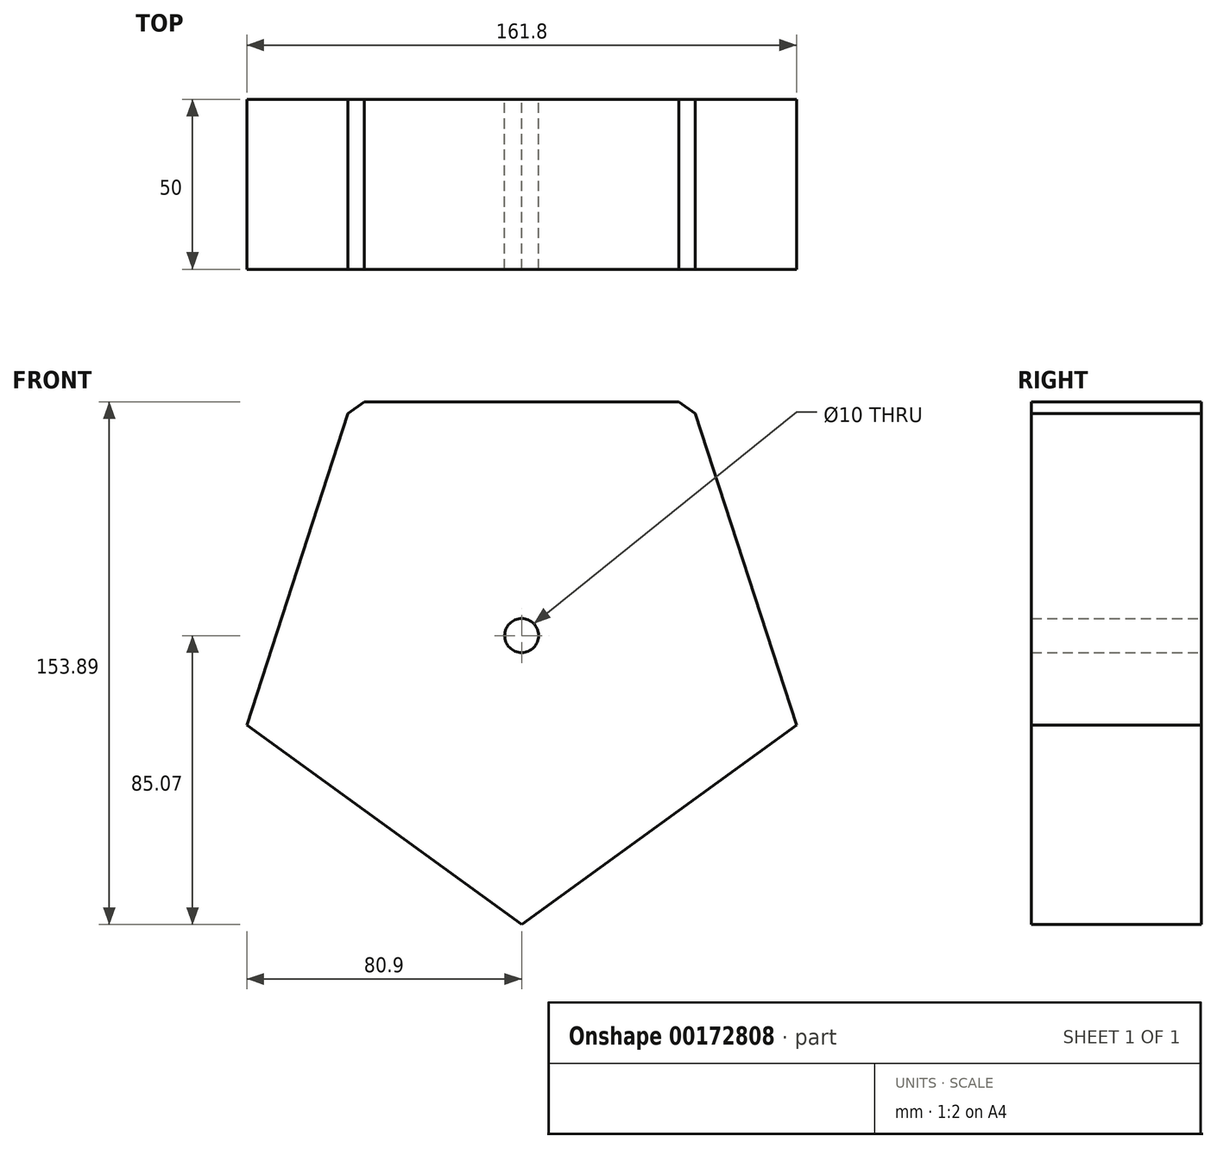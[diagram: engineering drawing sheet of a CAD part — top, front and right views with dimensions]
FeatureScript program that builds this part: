
annotation { "Feature Type Name" : "Feature", "Feature Type Description" : "" }
export const myFeature = defineFeature(function(context is Context, id is Id, definition is map)
    precondition{}
    {
        {
            var Q0;
            Q0=qCreatedBy(makeId("Front.planeOp"),FACE);
            var sketch = newSketch(context, id + "F0", { "sketchPlane" : qUnion([Q0])});
            skCircle(sketch, "E0.cCircle", {"center": v(0, 0) * mm, "radius": 68.82 * mm, "construction": true});
            skLineSegment(sketch, "E0.0", {"start": v(-50, 68.82) * mm, "end": v(50, 68.82) * mm});
            skLineSegment(sketch, "E0.1", {"start": v(50, 68.82) * mm, "end": v(80.9, -26.29) * mm});
            skLineSegment(sketch, "E0.2", {"start": v(80.9, -26.29) * mm, "end": v(0, -85.07) * mm});
            skLineSegment(sketch, "E0.3", {"start": v(0, -85.07) * mm, "end": v(-80.9, -26.29) * mm});
            skLineSegment(sketch, "E0.4", {"start": v(-80.9, -26.29) * mm, "end": v(-50, 68.82) * mm});
            skPoint(sketch, "E0.0.midPoint", {"position": v(0, 68.82) * mm});
            skSolve(sketch);
        }
        {
            var Q0;
            Q0=makeQuery(id+"F0.imprint","IMPRINT",FACE,{"disambiguationData":[TD([[makeQuery(id+"F0.imprint","IMPRINT",EDGE,{"derivedFrom":sQuery(id+"F0.wireOp",EDGE,"E0.0")}),-1.0]])]});
            extrude(context, id + "F1", {"entities" : qUnion([Q0]), "depth" : 50 * mm});
        }
        {
            var Q0;
            Q0=makeQuery(id+"F1.opExtrude","CAP_FACE",FACE,{"disambiguationData":[OSD([sQuery(id+"F0.wireOp",EDGE,"E0.0"),sQuery(id+"F0.wireOp",EDGE,"E0.1"),sQuery(id+"F0.wireOp",EDGE,"E0.2"),sQuery(id+"F0.wireOp",EDGE,"E0.3"),sQuery(id+"F0.wireOp",EDGE,"E0.4")])],"isStart":true});
            var sketch = newSketch(context, id + "F2", { "sketchPlane" : qUnion([Q0])});
            skPoint(sketch, "E1.0", {"position": v(0, 0) * mm});
            skSolve(sketch);
        }
        {
            var Q0;
            Q0=sQuery(id+"F2.wireOp",VERTEX,"E1.0");
            var Q1;
            Q1=makeQuery(id+"F1.opExtrude","SWEPT_BODY",BODY,{"disambiguationData":[OSD([sQuery(id+"F0.wireOp",EDGE,"E0.0"),sQuery(id+"F0.wireOp",EDGE,"E0.1"),sQuery(id+"F0.wireOp",EDGE,"E0.2"),sQuery(id+"F0.wireOp",EDGE,"E0.3"),sQuery(id+"F0.wireOp",EDGE,"E0.4")])]});
            hole(context, id + "F3", {"style" : HoleStyle.SIMPLE, "endStyle" : HoleEndStyle.THROUGH, "holeDiameter" : 10 * mm, "locations" : qUnion([Q0]), "scope" : qUnion([Q1]), "isTappedThrough" : true});
        }
        {
            var Q0;
            Q0=makeQuery(id+"F1.opExtrude","SWEPT_EDGE",EDGE,{"disambiguationData":[OSD([sQuery(id+"F0.wireOp",EDGE,"E0.0"),sQuery(id+"F0.wireOp",EDGE,"E0.4")])]});
            chamfer(context, id + "F4", {"entities" : qUnion([Q0]), "width" : 5 * mm, "tangentPropagation" : true});
        }
        {
            var Q0;
            Q0=makeQuery(id+"F1.opExtrude","SWEPT_EDGE",EDGE,{"disambiguationData":[OSD([sQuery(id+"F0.wireOp",EDGE,"E0.0"),sQuery(id+"F0.wireOp",EDGE,"E0.1")])]});
            chamfer(context, id + "F5", {"entities" : qUnion([Q0]), "width" : 5.08 * mm, "tangentPropagation" : true});
        }
    });
